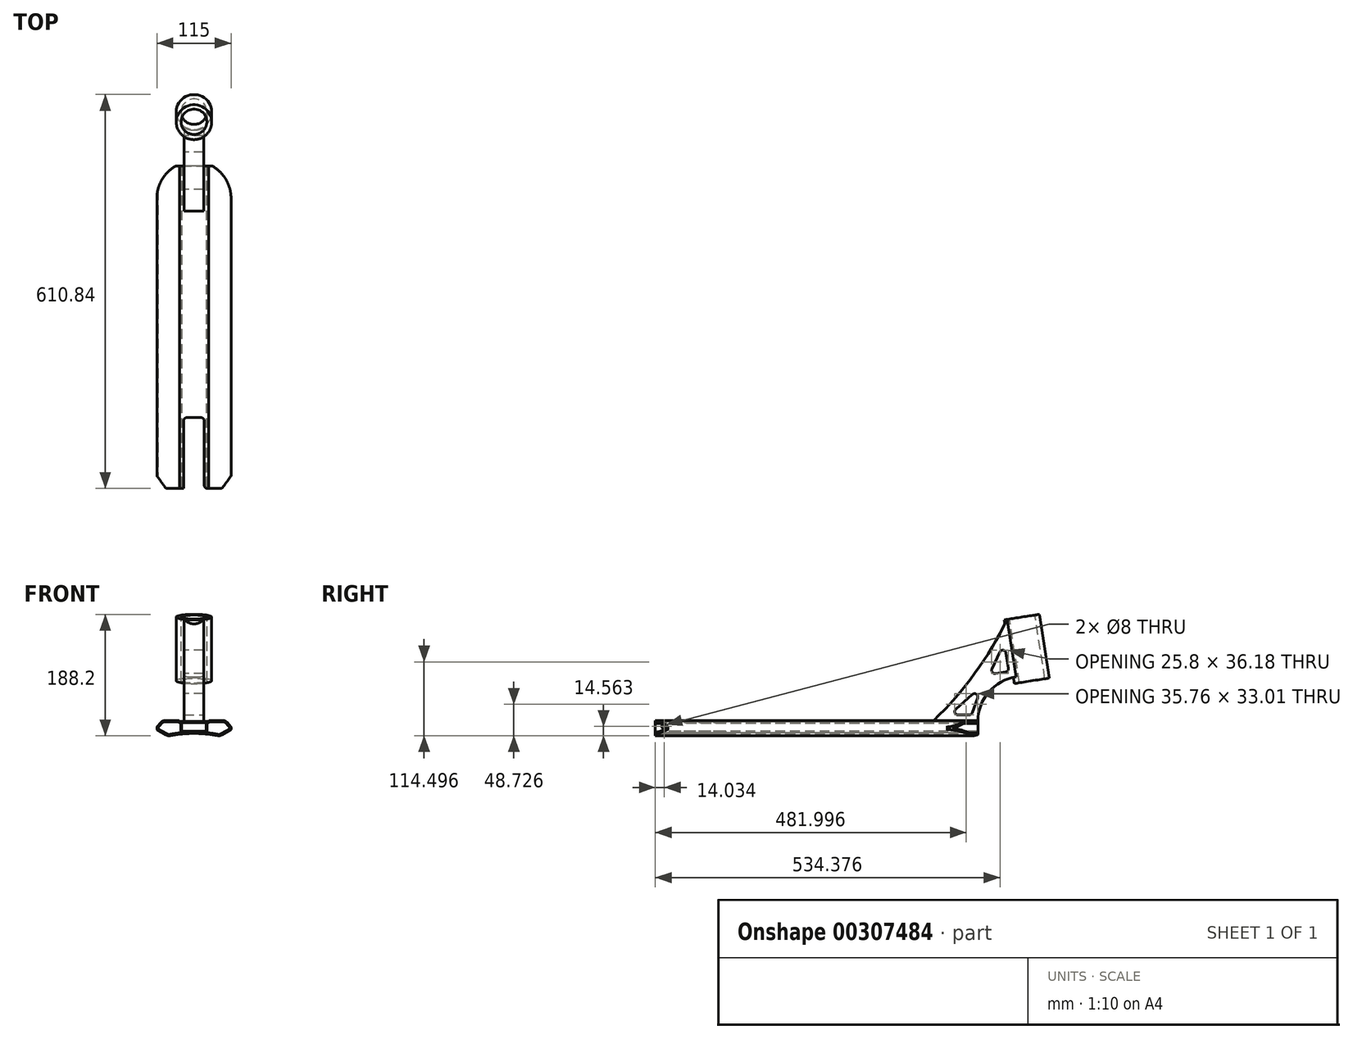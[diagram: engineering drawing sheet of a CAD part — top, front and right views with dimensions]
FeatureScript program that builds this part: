
annotation { "Feature Type Name" : "Feature", "Feature Type Description" : "" }
export const myFeature = defineFeature(function(context is Context, id is Id, definition is map)
    precondition{}
    {
        {
            var Q0;
            Q0=qCreatedBy(makeId("Front.planeOp"),FACE);
            var sketch = newSketch(context, id + "F0", { "sketchPlane" : qUnion([Q0])});
            skLineSegment(sketch, "E0", {"start": v(0, 0) * mm, "end": v(0, 15) * mm, "construction": true});
            skLineSegment(sketch, "E1", {"start": v(0, 0) * mm, "end": v(22.5, 0) * mm});
            skLineSegment(sketch, "E2", {"start": v(22.5, 0) * mm, "end": v(22.5, 1.3) * mm});
            skLineSegment(sketch, "E3", {"start": v(22.5, 1.3) * mm, "end": v(49.1, 1.3) * mm});
            skLineSegment(sketch, "E4", {"start": v(49.1, 1.3) * mm, "end": v(57.5, -8.7) * mm});
            skLineSegment(sketch, "E5", {"start": v(57.5, -8.7) * mm, "end": v(57.5, -12.7) * mm});
            skLineSegment(sketch, "E6", {"start": v(57.5, -12.7) * mm, "end": v(40.18, -22.7) * mm});
            skLineSegment(sketch, "E7.MirrorCS", {"start": v(0, 0) * mm, "end": v(-22.5, 0) * mm});
            skLineSegment(sketch, "E8.MirrorCS", {"start": v(-22.5, 1.3) * mm, "end": v(-49.1, 1.3) * mm});
            skLineSegment(sketch, "E9.MirrorCS", {"start": v(-22.5, 0) * mm, "end": v(-22.5, 1.3) * mm});
            skLineSegment(sketch, "E10.MirrorCS", {"start": v(-49.1, 1.3) * mm, "end": v(-57.5, -8.7) * mm});
            skLineSegment(sketch, "E11.MirrorCS", {"start": v(-57.5, -8.7) * mm, "end": v(-57.5, -12.7) * mm});
            skLineSegment(sketch, "E12.MirrorCS", {"start": v(-57.5, -12.7) * mm, "end": v(-40.18, -22.7) * mm});
            skArc(sketch, "E13", {"start": v(40.18, -22.7) * mm, "mid": v(0, -18.62) * mm, "end": v(-40.18, -22.7) * mm});
            skSolve(sketch);
        }
        {
            var Q0;
            Q0=makeQuery(id+"F0.imprint","IMPRINT",FACE,{"disambiguationData":[TD([[makeQuery(id+"F0.imprint","IMPRINT",EDGE,{"derivedFrom":sQuery(id+"F0.wireOp",EDGE,"E1")}),-1.0]])]});
            extrude(context, id + "F1", {"entities" : qUnion([Q0]), "endBound" : BoundingType.SYMMETRIC, "depth" : 500 * mm});
        }
        {
            var Q0;
            Q0=qCreatedBy(makeId("Front.planeOp"),FACE);
            var sketch = newSketch(context, id + "F2", { "sketchPlane" : qUnion([Q0])});
            skLineSegment(sketch, "E14.bottom", {"start": v(-19, -2) * mm, "end": v(19, -2) * mm});
            skLineSegment(sketch, "E14.top", {"start": v(-19, -15) * mm, "end": v(19, -15) * mm});
            skLineSegment(sketch, "E14.left", {"start": v(-19, -2) * mm, "end": v(-19, -15) * mm});
            skLineSegment(sketch, "E14.right", {"start": v(19, -2) * mm, "end": v(19, -15) * mm});
            skSolve(sketch);
        }
        {
            var Q0;
            Q0 = qSketchRegion(id + "F2", true);
            extrude(context, id + "F3", {"entities" : qUnion([Q0]), "operationType" : NewBodyOperationType.REMOVE, "endBound" : BoundingType.SYMMETRIC, "oppositeDirection" : true, "depth" : 500 * mm});
        }
        {
            var Q0;
            Q0=makeQuery(id+"F1.opExtrude","SWEPT_EDGE",EDGE,{"disambiguationData":[OSD([sQuery(id+"F0.wireOp",EDGE,"E8.MirrorCS"),sQuery(id+"F0.wireOp",EDGE,"E9.MirrorCS")])]});
            var Q1;
            Q1=makeQuery(id+"F1.opExtrude","SWEPT_EDGE",EDGE,{"disambiguationData":[OSD([sQuery(id+"F0.wireOp",EDGE,"E2"),sQuery(id+"F0.wireOp",EDGE,"E3")])]});
            fillet(context, id + "F4", {"entities" : qUnion([Q0, Q1]), "radius" : 2 * mm, "tangentPropagation" : true, "allowEdgeOverflow" : false});
        }
        {
            var Q0;
            Q0=makeQuery(id+"F1.opExtrude","SWEPT_EDGE",EDGE,{"disambiguationData":[OSD([sQuery(id+"F0.wireOp",EDGE,"E8.MirrorCS"),sQuery(id+"F0.wireOp",EDGE,"E10.MirrorCS")])]});
            var Q1;
            Q1=makeQuery(id+"F1.opExtrude","SWEPT_EDGE",EDGE,{"disambiguationData":[OSD([sQuery(id+"F0.wireOp",EDGE,"E3"),sQuery(id+"F0.wireOp",EDGE,"E4")])]});
            var Q2;
            Q2=makeQuery(id+"F1.opExtrude","SWEPT_EDGE",EDGE,{"disambiguationData":[OSD([sQuery(id+"F0.wireOp",EDGE,"E12.MirrorCS"),sQuery(id+"F0.wireOp",EDGE,"E13")])]});
            var Q3;
            Q3=makeQuery(id+"F1.opExtrude","SWEPT_EDGE",EDGE,{"disambiguationData":[OSD([sQuery(id+"F0.wireOp",EDGE,"E6"),sQuery(id+"F0.wireOp",EDGE,"E13")])]});
            fillet(context, id + "F5", {"entities" : qUnion([Q0, Q1, Q2, Q3]), "radius" : 9 * mm, "tangentPropagation" : true, "allowEdgeOverflow" : false});
        }
        {
            var Q0;
            Q0=makeQuery(id+"F1.opExtrude","SWEPT_EDGE",EDGE,{"disambiguationData":[OSD([sQuery(id+"F0.wireOp",EDGE,"E4"),sQuery(id+"F0.wireOp",EDGE,"E5")])]});
            var Q1;
            Q1=makeQuery(id+"F1.opExtrude","SWEPT_EDGE",EDGE,{"disambiguationData":[OSD([sQuery(id+"F0.wireOp",EDGE,"E5"),sQuery(id+"F0.wireOp",EDGE,"E6")])]});
            var Q2;
            Q2=makeQuery(id+"F1.opExtrude","SWEPT_EDGE",EDGE,{"disambiguationData":[OSD([sQuery(id+"F0.wireOp",EDGE,"E10.MirrorCS"),sQuery(id+"F0.wireOp",EDGE,"E11.MirrorCS")])]});
            var Q3;
            Q3=makeQuery(id+"F1.opExtrude","SWEPT_EDGE",EDGE,{"disambiguationData":[OSD([sQuery(id+"F0.wireOp",EDGE,"E11.MirrorCS"),sQuery(id+"F0.wireOp",EDGE,"E12.MirrorCS")])]});
            fillet(context, id + "F6", {"entities" : qUnion([Q0, Q1, Q2, Q3]), "radius" : 1 * mm, "tangentPropagation" : true, "allowEdgeOverflow" : false});
        }
        {
            var Q0;
            Q0=makeQuery(id+"F1.opExtrude","CAP_FACE",FACE,{"disambiguationData":[OSD([sQuery(id+"F0.wireOp",EDGE,"E1"),sQuery(id+"F0.wireOp",EDGE,"E2"),sQuery(id+"F0.wireOp",EDGE,"E3"),sQuery(id+"F0.wireOp",EDGE,"E4"),sQuery(id+"F0.wireOp",EDGE,"E5"),sQuery(id+"F0.wireOp",EDGE,"E6"),sQuery(id+"F0.wireOp",EDGE,"E7.MirrorCS"),sQuery(id+"F0.wireOp",EDGE,"E8.MirrorCS"),sQuery(id+"F0.wireOp",EDGE,"E9.MirrorCS"),sQuery(id+"F0.wireOp",EDGE,"E10.MirrorCS"),sQuery(id+"F0.wireOp",EDGE,"E11.MirrorCS"),sQuery(id+"F0.wireOp",EDGE,"E12.MirrorCS"),sQuery(id+"F0.wireOp",EDGE,"E13")])],"isStart":false});
            var sketch = newSketch(context, id + "F7", { "sketchPlane" : qUnion([Q0])});
            skArc(sketch, "E15.0", {"start": v(-20.42, -17.66) * mm, "mid": v(-28.9, -18.7) * mm, "end": v(-37.3, -20.1) * mm});
            skArc(sketch, "E15.1", {"start": v(-42.1, -19.28) * mm, "mid": v(-39.78, -20.12) * mm, "end": v(-37.3, -20.1) * mm});
            skLineSegment(sketch, "E15.2", {"start": v(-24.37, -0.7) * mm, "end": v(-44.91, -0.7) * mm});
            skArc(sketch, "E15.3", {"start": v(-44.91, -0.7) * mm, "mid": v(-47.87, -1.36) * mm, "end": v(-50.27, -3.2) * mm});
            skLineSegment(sketch, "E15.4", {"start": v(-50.27, -3.2) * mm, "end": v(-55.93, -9.94) * mm});
            skLineSegment(sketch, "E15.5", {"start": v(-55.66, -11.45) * mm, "end": v(-42.1, -19.28) * mm});
            skPoint(sketch, "E16.visualSharp", {"position": v(-56.7, -10.85) * mm});
            skArc(sketch, "E16.filletArc", {"start": v(-55.93, -9.94) * mm, "mid": v(-56.15, -10.76) * mm, "end": v(-55.66, -11.45) * mm});
            skArc(sketch, "E17", {"start": v(-24.37, -0.7) * mm, "mid": v(-22.81, -1.45) * mm, "end": v(-22.42, -3.13) * mm});
            skLineSegment(sketch, "E18", {"start": v(-22.42, -3.13) * mm, "end": v(-20.42, -3.13) * mm});
            skLineSegment(sketch, "E19", {"start": v(-20.42, -3.13) * mm, "end": v(-20.42, -17.66) * mm});
            skLineSegment(sketch, "E20", {"start": v(0, 0) * mm, "end": v(0, 10.77) * mm, "construction": true});
            skLineSegment(sketch, "E21.MirrorCS", {"start": v(20.42, -3.13) * mm, "end": v(20.42, -17.66) * mm});
            skLineSegment(sketch, "E22.MirrorCS", {"start": v(24.37, -0.7) * mm, "end": v(44.91, -0.7) * mm});
            skArc(sketch, "E23.MirrorCS", {"start": v(24.37, -0.7) * mm, "mid": v(22.81, -1.45) * mm, "end": v(22.42, -3.13) * mm});
            skLineSegment(sketch, "E24.MirrorCS", {"start": v(22.42, -3.13) * mm, "end": v(20.42, -3.13) * mm});
            skArc(sketch, "E25.MirrorCS", {"start": v(44.91, -0.7) * mm, "mid": v(47.87, -1.36) * mm, "end": v(50.27, -3.2) * mm});
            skLineSegment(sketch, "E26.MirrorCS", {"start": v(50.27, -3.2) * mm, "end": v(55.93, -9.94) * mm});
            skArc(sketch, "E27.MirrorCS", {"start": v(55.93, -9.94) * mm, "mid": v(56.15, -10.76) * mm, "end": v(55.66, -11.45) * mm});
            skLineSegment(sketch, "E28.MirrorCS", {"start": v(55.66, -11.45) * mm, "end": v(42.1, -19.28) * mm});
            skArc(sketch, "E29.MirrorCS", {"start": v(42.1, -19.28) * mm, "mid": v(39.78, -20.12) * mm, "end": v(37.3, -20.1) * mm});
            skArc(sketch, "E30.MirrorCS", {"start": v(20.42, -17.66) * mm, "mid": v(28.9, -18.7) * mm, "end": v(37.3, -20.1) * mm});
            skSolve(sketch);
        }
        {
            var Q0;
            Q0 = qSketchRegion(id + "F7", true);
            extrude(context, id + "F8", {"entities" : qUnion([Q0]), "operationType" : NewBodyOperationType.REMOVE, "endBound" : BoundingType.THROUGH_ALL, "oppositeDirection" : true, "depth" : 25 * mm});
        }
        {
            var Q0;
            Q0=qCreatedBy(makeId("Top.planeOp"),FACE);
            var sketch = newSketch(context, id + "F9", { "sketchPlane" : qUnion([Q0])});
            skArc(sketch, "E31", {"start": v(57.5, 200.37) * mm, "mid": v(0, 257.5) * mm, "end": v(-57.5, 200.37) * mm});
            skLineSegment(sketch, "E32", {"start": v(57.5, 200.37) * mm, "end": v(57.5, 280.37) * mm});
            skLineSegment(sketch, "E33", {"start": v(-57.5, 200.37) * mm, "end": v(-57.5, 280.37) * mm});
            skLineSegment(sketch, "E34", {"start": v(-57.5, 280.37) * mm, "end": v(57.5, 280.37) * mm});
            skSolve(sketch);
        }
        {
            var Q0;
            Q0 = qSketchRegion(id + "F9", true);
            extrude(context, id + "F10", {"entities" : qUnion([Q0]), "operationType" : NewBodyOperationType.REMOVE, "endBound" : BoundingType.THROUGH_ALL, "oppositeDirection" : true, "depth" : 25 * mm, "hasSecondDirection" : true, "secondDirectionBound" : SecondDirectionBoundingType.THROUGH_ALL, "secondDirectionOppositeDirection" : false, "secondDirectionDepth" : 25 * mm});
        }
        {
            var Q0;
            Q0=qCreatedBy(makeId("Top.planeOp"),FACE);
            var sketch = newSketch(context, id + "F11", { "sketchPlane" : qUnion([Q0])});
            skLineSegment(sketch, "E35", {"start": v(-68, -216) * mm, "end": v(-68, -346) * mm});
            skLineSegment(sketch, "E36", {"start": v(-68, -346) * mm, "end": v(68, -346) * mm});
            skLineSegment(sketch, "E37", {"start": v(68, -346) * mm, "end": v(68, -216) * mm});
            skLineSegment(sketch, "E38", {"start": v(68, -216) * mm, "end": v(43.3, -250) * mm});
            skLineSegment(sketch, "E39", {"start": v(43.3, -250) * mm, "end": v(16, -250) * mm});
            skLineSegment(sketch, "E40", {"start": v(16, -250) * mm, "end": v(16, -140) * mm});
            skLineSegment(sketch, "E41", {"start": v(16, -140) * mm, "end": v(-16, -140) * mm});
            skLineSegment(sketch, "E42", {"start": v(-16, -140) * mm, "end": v(-16, -250) * mm});
            skLineSegment(sketch, "E43", {"start": v(-16, -250) * mm, "end": v(-43.3, -250) * mm});
            skLineSegment(sketch, "E44", {"start": v(-43.3, -250) * mm, "end": v(-68, -216) * mm});
            skSolve(sketch);
        }
        {
            var Q0;
            Q0 = qSketchRegion(id + "F11", true);
            extrude(context, id + "F12", {"entities" : qUnion([Q0]), "operationType" : NewBodyOperationType.REMOVE, "endBound" : BoundingType.THROUGH_ALL, "oppositeDirection" : true, "depth" : 25 * mm, "hasSecondDirection" : true, "secondDirectionBound" : SecondDirectionBoundingType.THROUGH_ALL, "secondDirectionOppositeDirection" : false, "secondDirectionDepth" : 25 * mm});
        }
        {
            var Q0;
            {var subQ0=sQuery(id+"F0.wireOp",EDGE,"E13");var subQ1=sQuery(id+"F11.wireOp",EDGE,"E42");Q0=makeQuery(id+"F12.boolean.opBoolean","COPY",EDGE,{"disambiguationData":[TD([makeQuery(id+"F1.opExtrude","SWEPT_FACE",FACE,{"disambiguationData":[OSD([subQ0])]})])],"derivedFrom":makeQuery(id+"F12.opExtrude","SWEPT_EDGE",EDGE,{"disambiguationData":[OSD([subQ1,sQuery(id+"F11.wireOp",EDGE,"E43")])]})});}
            var Q1;
            {var subQ0=sQuery(id+"F11.wireOp",EDGE,"E41");var subQ1=sQuery(id+"F11.wireOp",EDGE,"E42");Q1=makeQuery(id+"F12.boolean.opBoolean","COPY",EDGE,{"disambiguationData":[TD([makeQuery(id+"F3.boolean.opBoolean","COPY",FACE,{"derivedFrom":makeQuery(id+"F3.opExtrude","SWEPT_FACE",FACE,{"disambiguationData":[OSD([sQuery(id+"F2.wireOp",EDGE,"E14.bottom")])]})})])],"derivedFrom":makeQuery(id+"F12.opExtrude","SWEPT_EDGE",EDGE,{"disambiguationData":[OSD([subQ0,subQ1])]})});}
            var Q2;
            {var subQ0=sQuery(id+"F11.wireOp",EDGE,"E41");var subQ1=sQuery(id+"F11.wireOp",EDGE,"E42");Q2=makeQuery(id+"F12.boolean.opBoolean","COPY",EDGE,{"disambiguationData":[TD([makeQuery(id+"F1.opExtrude","SWEPT_FACE",FACE,{"disambiguationData":[OSD([sQuery(id+"F0.wireOp",EDGE,"E13")])]})])],"derivedFrom":makeQuery(id+"F12.opExtrude","SWEPT_EDGE",EDGE,{"disambiguationData":[OSD([subQ0,subQ1])]})});}
            var Q3;
            {var subQ0=sQuery(id+"F0.wireOp",EDGE,"E13");var subQ1=sQuery(id+"F11.wireOp",EDGE,"E40");Q3=makeQuery(id+"F12.boolean.opBoolean","COPY",EDGE,{"disambiguationData":[TD([makeQuery(id+"F1.opExtrude","SWEPT_FACE",FACE,{"disambiguationData":[OSD([subQ0])]})])],"derivedFrom":makeQuery(id+"F12.opExtrude","SWEPT_EDGE",EDGE,{"disambiguationData":[OSD([sQuery(id+"F11.wireOp",EDGE,"E39"),subQ1])]})});}
            var Q4;
            {var subQ0=sQuery(id+"F11.wireOp",EDGE,"E40");var subQ1=sQuery(id+"F11.wireOp",EDGE,"E41");Q4=makeQuery(id+"F12.boolean.opBoolean","COPY",EDGE,{"disambiguationData":[TD([makeQuery(id+"F3.boolean.opBoolean","COPY",FACE,{"derivedFrom":makeQuery(id+"F3.opExtrude","SWEPT_FACE",FACE,{"disambiguationData":[OSD([sQuery(id+"F2.wireOp",EDGE,"E14.bottom")])]})})])],"derivedFrom":makeQuery(id+"F12.opExtrude","SWEPT_EDGE",EDGE,{"disambiguationData":[OSD([subQ0,subQ1])]})});}
            var Q5;
            {var subQ0=sQuery(id+"F11.wireOp",EDGE,"E41");var subQ1=sQuery(id+"F11.wireOp",EDGE,"E40");Q5=makeQuery(id+"F12.boolean.opBoolean","COPY",EDGE,{"disambiguationData":[TD([makeQuery(id+"F1.opExtrude","SWEPT_FACE",FACE,{"disambiguationData":[OSD([sQuery(id+"F0.wireOp",EDGE,"E13")])]})])],"derivedFrom":makeQuery(id+"F12.opExtrude","SWEPT_EDGE",EDGE,{"disambiguationData":[OSD([subQ1,subQ0])]})});}
            fillet(context, id + "F13", {"entities" : qUnion([Q0, Q1, Q2, Q3, Q4, Q5]), "radius" : 5 * mm, "tangentPropagation" : true, "allowEdgeOverflow" : false});
        }
        {
            var Q0;
            Q0=qCreatedBy(makeId("Right.planeOp"),FACE);
            var sketch = newSketch(context, id + "F14", { "sketchPlane" : qUnion([Q0])});
            skLineSegment(sketch, "E45", {"start": v(180, 0) * mm, "end": v(250, 0) * mm});
            skLineSegment(sketch, "E46", {"start": v(356.44, 66.51) * mm, "end": v(340.8, 165.28) * mm});
            skLineSegment(sketch, "E47", {"start": v(340.8, 165.28) * mm, "end": v(295.36, 158.09) * mm});
            skArc(sketch, "E48", {"start": v(180, 0) * mm, "mid": v(244.77, 73.87) * mm, "end": v(295.36, 158.09) * mm});
            skArc(sketch, "E49", {"start": v(309.44, 69.2) * mm, "mid": v(266.9, 45.61) * mm, "end": v(250, 0) * mm});
            skLineSegment(sketch, "E50", {"start": v(309.44, 69.2) * mm, "end": v(311, 59.32) * mm});
            skLineSegment(sketch, "E51", {"start": v(311, 59.32) * mm, "end": v(356.44, 66.51) * mm});
            skSolve(sketch);
        }
        {
            var Q0;
            Q0 = qSketchRegion(id + "F14", true);
            extrude(context, id + "F15", {"entities" : qUnion([Q0]), "operationType" : NewBodyOperationType.ADD, "endBound" : BoundingType.SYMMETRIC, "depth" : 30 * mm});
        }
        {
            var Q0;
            Q0=makeQuery(id+"F15.opExtrude","SWEPT_FACE",FACE,{"disambiguationData":[OSD([sQuery(id+"F14.wireOp",EDGE,"E47")])]});
            var sketch = newSketch(context, id + "F16", { "sketchPlane" : qUnion([Q0])});
            skCircle(sketch, "E52", {"center": v(0, 339.46) * mm, "radius": 27.46 * mm});
            skSolve(sketch);
        }
        {
            var Q0;
            Q0 = qSketchRegion(id + "F16", true);
            var Q1;
            Q1=makeQuery(id+"F15.opExtrude","SWEPT_FACE",FACE,{"disambiguationData":[OSD([sQuery(id+"F14.wireOp",EDGE,"E51")])]});
            extrude(context, id + "F17", {"entities" : qUnion([Q0]), "operationType" : NewBodyOperationType.ADD, "endBound" : BoundingType.UP_TO_SURFACE, "oppositeDirection" : true, "endBoundEntityFace" : qUnion([Q1]), "depth" : 25 * mm});
        }
        {
            var Q0;
            Q0=makeQuery(id+"F17.boolean.opBoolean","MERGE",FACE,{"derivedFrom":[makeQuery(id+"F15.opExtrude","SWEPT_FACE",FACE,{"disambiguationData":[OSD([sQuery(id+"F14.wireOp",EDGE,"E47")])]}),makeQuery(id+"F17.opExtrude","CAP_FACE",FACE,{"disambiguationData":[OSD([sQuery(id+"F16.wireOp",EDGE,"E52")])],"isStart":true})]});
            var sketch = newSketch(context, id + "F18", { "sketchPlane" : qUnion([Q0])});
            skSolve(sketch);
        }
        {
            var Q0;
            {var subQ0=makeQuery(id+"F17.opExtrude","CAP_EDGE",EDGE,{"disambiguationData":[OSD([sQuery(id+"F16.wireOp",EDGE,"E52")])],"isStart":true});Q0=makeQuery(id+"F18.imprint","IMPRINT",FACE,{"disambiguationData":[TD([[makeQuery(id+"F18.imprint","IMPRINT",EDGE,{"derivedFrom":makeQuery(id+"F17.boolean.opBoolean","SPLIT",EDGE,{"disambiguationData":[OD(0.0)],"derivedFrom":subQ0})}),1.0]])]});}
            var sketch = newSketch(context, id + "F19", { "sketchPlane" : qUnion([Q0])});
            skPoint(sketch, "E53", {"position": v(0, 340.02) * mm});
            skSolve(sketch);
        }
        {
            var Q0;
            Q0=sQuery(id+"F19.wireOp",VERTEX,"E53");
            var Q1;
            Q1=makeQuery(id+"F1.opExtrude","SWEPT_BODY",BODY,{"disambiguationData":[OSD([sQuery(id+"F0.wireOp",EDGE,"E1"),sQuery(id+"F0.wireOp",EDGE,"E2"),sQuery(id+"F0.wireOp",EDGE,"E3"),sQuery(id+"F0.wireOp",EDGE,"E4"),sQuery(id+"F0.wireOp",EDGE,"E5"),sQuery(id+"F0.wireOp",EDGE,"E6"),sQuery(id+"F0.wireOp",EDGE,"E7.MirrorCS"),sQuery(id+"F0.wireOp",EDGE,"E8.MirrorCS"),sQuery(id+"F0.wireOp",EDGE,"E9.MirrorCS"),sQuery(id+"F0.wireOp",EDGE,"E10.MirrorCS"),sQuery(id+"F0.wireOp",EDGE,"E11.MirrorCS"),sQuery(id+"F0.wireOp",EDGE,"E12.MirrorCS"),sQuery(id+"F0.wireOp",EDGE,"E13")])]});
            hole(context, id + "F20", {"style" : HoleStyle.SIMPLE, "endStyle" : HoleEndStyle.THROUGH, "holeDiameter" : 40 * mm, "isTappedThrough" : true, "tappedDepth" : 12 * mm, "tapClearance" : 3, "locations" : qUnion([Q0]), "scope" : qUnion([Q1])});
        }
        {
            var Q0;
            Q0=makeQuery(id+"F8.boolean.opBoolean","COPY",FACE,{"derivedFrom":makeQuery(id+"F8.opExtrude","SWEPT_FACE",FACE,{"disambiguationData":[OSD([sQuery(id+"F7.wireOp",EDGE,"E21.MirrorCS")])]})});
            var sketch = newSketch(context, id + "F21", { "sketchPlane" : qUnion([Q0])});
            skPoint(sketch, "E54", {"position": v(-235.97, -7.66) * mm});
            skSolve(sketch);
        }
        {
            var Q0;
            Q0=sQuery(id+"F21.wireOp",VERTEX,"E54");
            var Q1;
            Q1=makeQuery(id+"F1.opExtrude","SWEPT_BODY",BODY,{"disambiguationData":[OSD([sQuery(id+"F0.wireOp",EDGE,"E1"),sQuery(id+"F0.wireOp",EDGE,"E2"),sQuery(id+"F0.wireOp",EDGE,"E3"),sQuery(id+"F0.wireOp",EDGE,"E4"),sQuery(id+"F0.wireOp",EDGE,"E5"),sQuery(id+"F0.wireOp",EDGE,"E6"),sQuery(id+"F0.wireOp",EDGE,"E7.MirrorCS"),sQuery(id+"F0.wireOp",EDGE,"E8.MirrorCS"),sQuery(id+"F0.wireOp",EDGE,"E9.MirrorCS"),sQuery(id+"F0.wireOp",EDGE,"E10.MirrorCS"),sQuery(id+"F0.wireOp",EDGE,"E11.MirrorCS"),sQuery(id+"F0.wireOp",EDGE,"E12.MirrorCS"),sQuery(id+"F0.wireOp",EDGE,"E13")])]});
            hole(context, id + "F22", {"style" : HoleStyle.SIMPLE, "endStyle" : HoleEndStyle.BLIND, "holeDiameter" : 8 * mm, "holeDepth" : 60 * mm, "isTappedThrough" : true, "tappedDepth" : 12 * mm, "tapClearance" : 3, "locations" : qUnion([Q0]), "scope" : qUnion([Q1])});
        }
        {
            var Q0;
            Q0=makeQuery(id+"F15.opExtrude","CAP_FACE",FACE,{"disambiguationData":[OSD([sQuery(id+"F14.wireOp",EDGE,"E45"),sQuery(id+"F14.wireOp",EDGE,"E46"),sQuery(id+"F14.wireOp",EDGE,"E47"),sQuery(id+"F14.wireOp",EDGE,"E48"),sQuery(id+"F14.wireOp",EDGE,"E49"),sQuery(id+"F14.wireOp",EDGE,"E50"),sQuery(id+"F14.wireOp",EDGE,"E51")])],"isStart":false});
            var sketch = newSketch(context, id + "F23", { "sketchPlane" : qUnion([Q0])});
            skLineSegment(sketch, "E55", {"start": v(256.38, 55) * mm, "end": v(240, 10) * mm});
            skLineSegment(sketch, "E56", {"start": v(240, 10) * mm, "end": v(206, 10) * mm});
            skLineSegment(sketch, "E57", {"start": v(206, 10) * mm, "end": v(256.38, 55) * mm});
            skLineSegment(sketch, "E58", {"start": v(290.87, 122.5) * mm, "end": v(298, 77.5) * mm});
            skLineSegment(sketch, "E59", {"start": v(298, 77.5) * mm, "end": v(268, 72.75) * mm});
            skLineSegment(sketch, "E60", {"start": v(268, 72.75) * mm, "end": v(290.87, 122.5) * mm});
            skSolve(sketch);
        }
        {
            var Q0;
            Q0 = qSketchRegion(id + "F23", true);
            extrude(context, id + "F24", {"entities" : qUnion([Q0]), "operationType" : NewBodyOperationType.REMOVE, "endBound" : BoundingType.THROUGH_ALL, "oppositeDirection" : true, "depth" : 25 * mm});
        }
        {
            var Q0;
            Q0=makeQuery(id+"F24.boolean.opBoolean","COPY",EDGE,{"derivedFrom":makeQuery(id+"F24.opExtrude","SWEPT_EDGE",EDGE,{"disambiguationData":[OSD([sQuery(id+"F23.wireOp",EDGE,"E56"),sQuery(id+"F23.wireOp",EDGE,"E57")])]})});
            var Q1;
            Q1=makeQuery(id+"F24.boolean.opBoolean","COPY",EDGE,{"derivedFrom":makeQuery(id+"F24.opExtrude","SWEPT_EDGE",EDGE,{"disambiguationData":[OSD([sQuery(id+"F23.wireOp",EDGE,"E55"),sQuery(id+"F23.wireOp",EDGE,"E57")])]})});
            var Q2;
            Q2=makeQuery(id+"F24.boolean.opBoolean","COPY",EDGE,{"derivedFrom":makeQuery(id+"F24.opExtrude","SWEPT_EDGE",EDGE,{"disambiguationData":[OSD([sQuery(id+"F23.wireOp",EDGE,"E55"),sQuery(id+"F23.wireOp",EDGE,"E56")])]})});
            var Q3;
            Q3=makeQuery(id+"F24.boolean.opBoolean","COPY",EDGE,{"derivedFrom":makeQuery(id+"F24.opExtrude","SWEPT_EDGE",EDGE,{"disambiguationData":[OSD([sQuery(id+"F23.wireOp",EDGE,"E58"),sQuery(id+"F23.wireOp",EDGE,"E59")])]})});
            var Q4;
            Q4=makeQuery(id+"F24.boolean.opBoolean","COPY",EDGE,{"derivedFrom":makeQuery(id+"F24.opExtrude","SWEPT_EDGE",EDGE,{"disambiguationData":[OSD([sQuery(id+"F23.wireOp",EDGE,"E58"),sQuery(id+"F23.wireOp",EDGE,"E60")])]})});
            var Q5;
            Q5=makeQuery(id+"F24.boolean.opBoolean","COPY",EDGE,{"derivedFrom":makeQuery(id+"F24.opExtrude","SWEPT_EDGE",EDGE,{"disambiguationData":[OSD([sQuery(id+"F23.wireOp",EDGE,"E59"),sQuery(id+"F23.wireOp",EDGE,"E60")])]})});
            fillet(context, id + "F25", {"entities" : qUnion([Q0, Q1, Q2, Q3, Q4, Q5]), "radius" : 5 * mm, "tangentPropagation" : true, "allowEdgeOverflow" : false});
        }
    });
